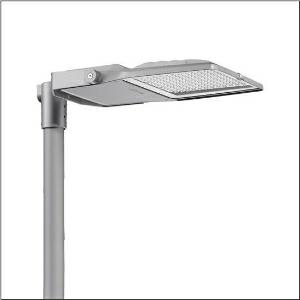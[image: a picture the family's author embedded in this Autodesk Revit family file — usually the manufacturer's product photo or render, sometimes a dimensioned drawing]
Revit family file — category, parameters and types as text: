
# Revit family: floodlight_fl_21_iq_midi___pl52_5xa7782f4d3a_fe87
name_source: partatom
category: Lighting Fixtures
units: mm (PartAtom-declared; Revit-internal decimal feet)

## family parameters
Cut with Voids When Loaded = No
Host = Face
Light Source = No
Part Type = Normal
Room Calculation Point = No
Round Connector Dimension = Use Diameter
Shared = No

## types (1)
- --- (1 x LED, 37330 lm, 270.2 W, 4000K)
    Apparent Load = 270 VA
    CIE Flux Codes = 26 60 98 100 100
    Color Rendering = 70
    Color Temperature = 4000K
    Default Elevation = 1800 mm
    Description = Floodlight FL 21 iQ midi, floodlight, primary light control with lens, of PMMA, primary optical cover: protective disc, of toughened safety glass, transparent, light distribution: PL52, light emission: direct distribution, installation type: surface-mounted, lamps: LED, High Power LED, rated values: 37.330lm | 270,2W | 138,2lm/W (begin service life); end service life: 37.330lm | 286,6W; at 50% lumin. flux: 18.665lm | 117,7W | 158,6lm/W, colour temperature: 4000K, colour rendering: CRI > 70, light colour: 740, light setting 1 begin service life: 100% | 37.330lm | 270,2W | 138,2lm/W | 4.000K, light setting 1 end service life: 286,6W, further light settings possible, control: optimised constant luminous flux control (CLO 2.0), Desk-Remote (wireless, voltage-free reading and setting of iQ features in the workshop via application-optimized NFC function/RFID function), Smart-Wire, Night-Set, Temp-Guard, Auto-Match, Street-Remote, pre-setting: linear dimming characteristic, with terminal, 6-pole, mains connection: 220..240V, AC, 50/60Hz, luminaire housing, of diecast aluminium, powder-coated, SITECO metallic grey (DB 702S), corrosivity category C5 mid according to DIN EN ISO 12944suitable for swimming poolschlorine-resistant, sealing non-destructively replaceable, please order mast flange separately, mast bracket, of steel, galvanised, powder-coated, SITECO metallic grey (DB 702S), protection rating (complete): IP66, insulation class (complete): insulation class II (safety insulation), certification: CE, ENEC, VDE, protection symbol: D, impact resistance: IK08, permissible operating ambient temperature: -40..+40°C, permissible operating ambient temperature for outdoor applications: -40..+50°C, standard: DIN EN 12944, LABS conformity tested according to VDMA 24364:2018-05, packaging unit: 1 piece

Light Distribution: PL52
    Height = 76 mm
    Lamp = 1 x LED
    Lamp Light Flux = 37330 lm
    Lamp Power = 270.2 W
    Lamp count = 1
    Length = 657 mm
    Luminous efficacy = 138 lm/W
    Manufacturer = Siteco
    ModVariant = No
    Model = 5XA7782F4D3A
    Number of Poles = 1
    OnlyDefault = Yes
    Power Factor = 1
    Product Name = Floodlight FL 21 iQ midi | PL52
    Product group = floodlight | pylon annexe
    ProductGroupID = 6201
    Protection Class = Protection class II
    Protection Degree = IP 66
    RLX_Detail_Level = 1
    RLX_Emergency_Light_Flux = 0 lm
    RLX_Emergency_Type = 0
    RLX_Emergency_Type_DB = No
    RlxData = <blob elided: 154105 chars, md5=d4e44367>
    Socket = socket
    Standby Power = 0 W
    System Light Flux = 37330 lm
    System Power = 270 W
    Type Comments = factory setting: luminous flux: 100 % | dim-lin: 254 | 620 mA
    Type Image = l_1007123.jpg
    URL = http://relux.com
    VarID = @adj_105467
    Voltage = 0 V
    Weight = 0.00 kg
    Width = 442 mm

## geometry (parser evidence)
native form markers: Blend x4, Sweep x15
no freeform markers — native parametric forms only
